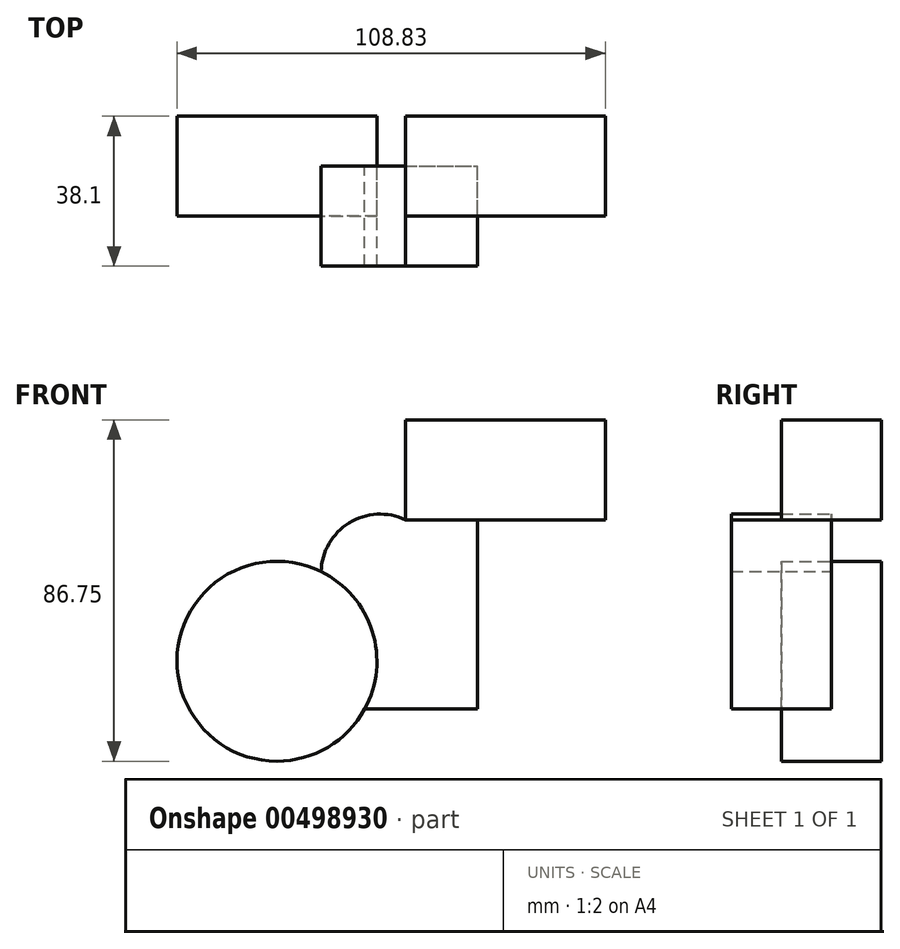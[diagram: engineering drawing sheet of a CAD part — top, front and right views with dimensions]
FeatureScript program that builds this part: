
annotation { "Feature Type Name" : "Feature", "Feature Type Description" : "" }
export const myFeature = defineFeature(function(context is Context, id is Id, definition is map)
    precondition{}
    {
        {
            var Q0;
            Q0=qCreatedBy(makeId("Front.planeOp"),FACE);
            var sketch = newSketch(context, id + "F0", { "sketchPlane" : qUnion([Q0])});
            skCircle(sketch, "E0", {"center": v(0, 0) * mm, "radius": 25.4 * mm});
            skLineSegment(sketch, "E1", {"start": v(12.9, -12.17) * mm, "end": v(51, -12.17) * mm});
            skLineSegment(sketch, "E2", {"start": v(51, -12.17) * mm, "end": v(51, 38.63) * mm});
            skLineSegment(sketch, "E3.bottom", {"start": v(32.63, 35.95) * mm, "end": v(83.43, 35.95) * mm});
            skLineSegment(sketch, "E3.top", {"start": v(32.63, 61.35) * mm, "end": v(83.43, 61.35) * mm});
            skLineSegment(sketch, "E3.left", {"start": v(32.63, 35.95) * mm, "end": v(32.63, 61.35) * mm});
            skLineSegment(sketch, "E3.right", {"start": v(83.43, 35.95) * mm, "end": v(83.43, 61.35) * mm});
            skArc(sketch, "E4", {"start": v(32.63, 35.95) * mm, "mid": v(18.37, 35.15) * mm, "end": v(11.22, 22.79) * mm});
            skSolve(sketch);
        }
        {
            var Q0;
            {var subQ0=sQuery(id+"F0.wireOp",EDGE,"E0");var subQ1=makeQuery(id+"F0.imprint","INTERSECT",VERTEX,{"derivedFrom":[subQ0,sQuery(id+"F0.wireOp",EDGE,"E4")]});Q0=makeQuery(id+"F0.imprint","IMPRINT",FACE,{"disambiguationData":[TD([[makeQuery(id+"F0.imprint","IMPRINT",EDGE,{"disambiguationData":[TD([[subQ1,-1.0]])],"derivedFrom":subQ0}),1.0]])]});}
            var Q1;
            Q1=makeQuery(id+"F0.imprint","IMPRINT",FACE,{"disambiguationData":[TD([[makeQuery(id+"F0.imprint","IMPRINT",EDGE,{"derivedFrom":sQuery(id+"F0.wireOp",EDGE,"E3.top")}),-1.0]])]});
            extrude(context, id + "F1", {"entities" : qUnion([Q0, Q1]), "endBound" : BoundingType.SYMMETRIC, "depth" : 25.4 * mm});
        }
        {
            var Q0;
            {var subQ0=sQuery(id+"F0.wireOp",EDGE,"E4");Q0=makeQuery(id+"F0.imprint","IMPRINT",FACE,{"disambiguationData":[TD([[makeQuery(id+"F0.imprint","IMPRINT",EDGE,{"derivedFrom":subQ0}),1.0]])]});}
            extrude(context, id + "F2", {"entities" : qUnion([Q0]), "depth" : 25.4 * mm});
        }
    });
